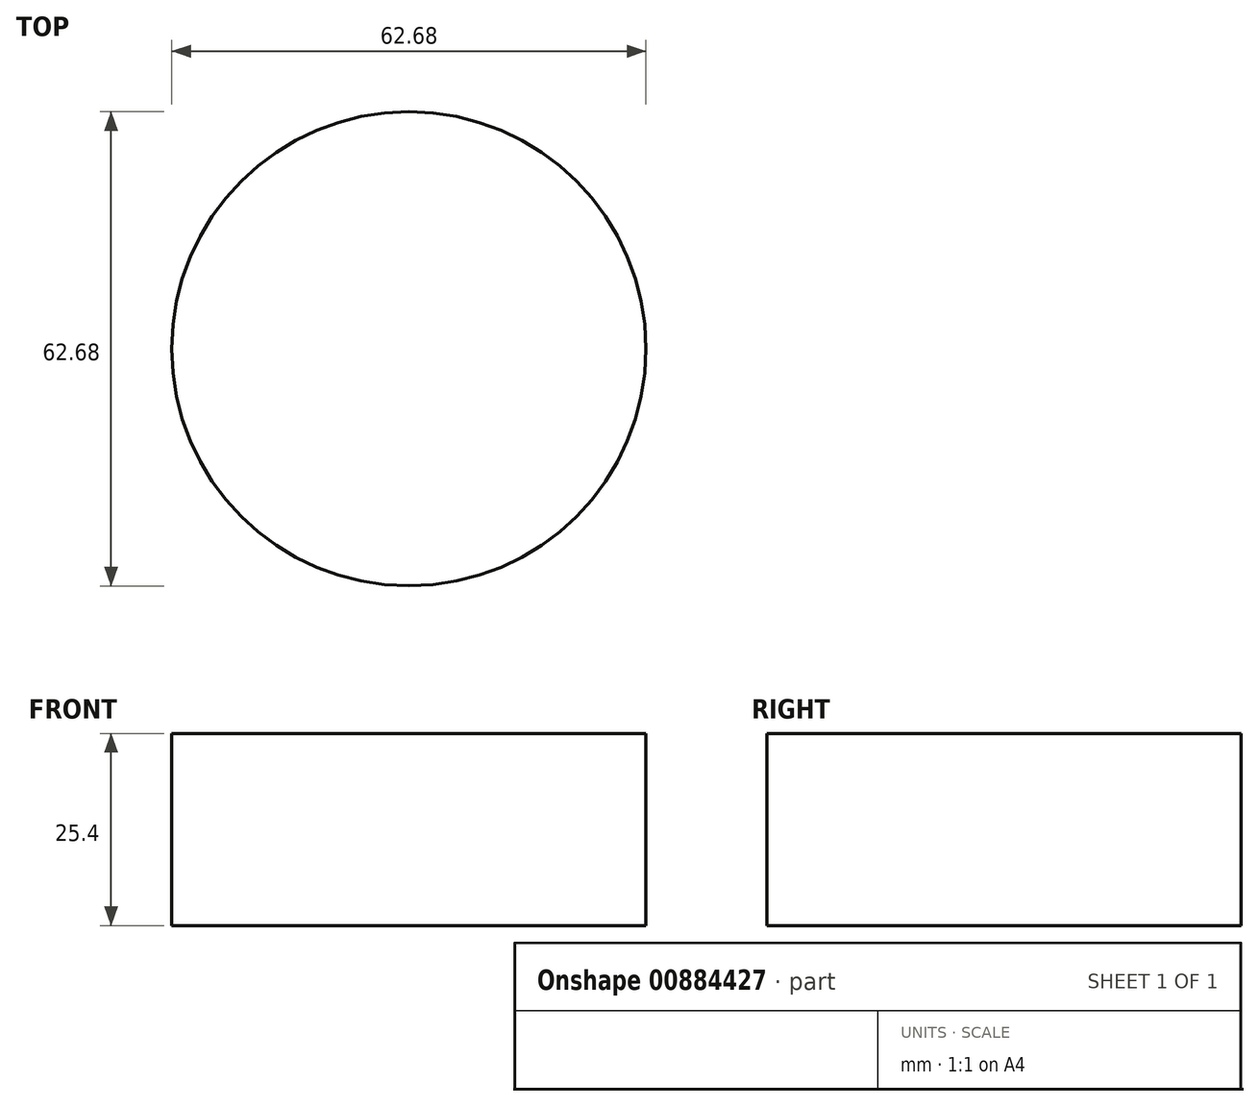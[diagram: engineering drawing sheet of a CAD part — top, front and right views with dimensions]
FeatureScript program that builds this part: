
annotation { "Feature Type Name" : "Feature", "Feature Type Description" : "" }
export const myFeature = defineFeature(function(context is Context, id is Id, definition is map)
    precondition{}
    {
        {
            var Q0;
            Q0=qCreatedBy(makeId("Top.planeOp"),FACE);
            var sketch = newSketch(context, id + "F0", { "sketchPlane" : qUnion([Q0])});
            skCircle(sketch, "E0", {"center": v(0, 0) * mm, "radius": 31.34 * mm});
            skSolve(sketch);
        }
        {
            var Q0;
            Q0 = qSketchRegion(id + "F0", true);
            extrude(context, id + "F1", {"entities" : qUnion([Q0]), "depth" : 25.4 * mm, "offsetDistance" : 25.4 * mm});
        }
    });
